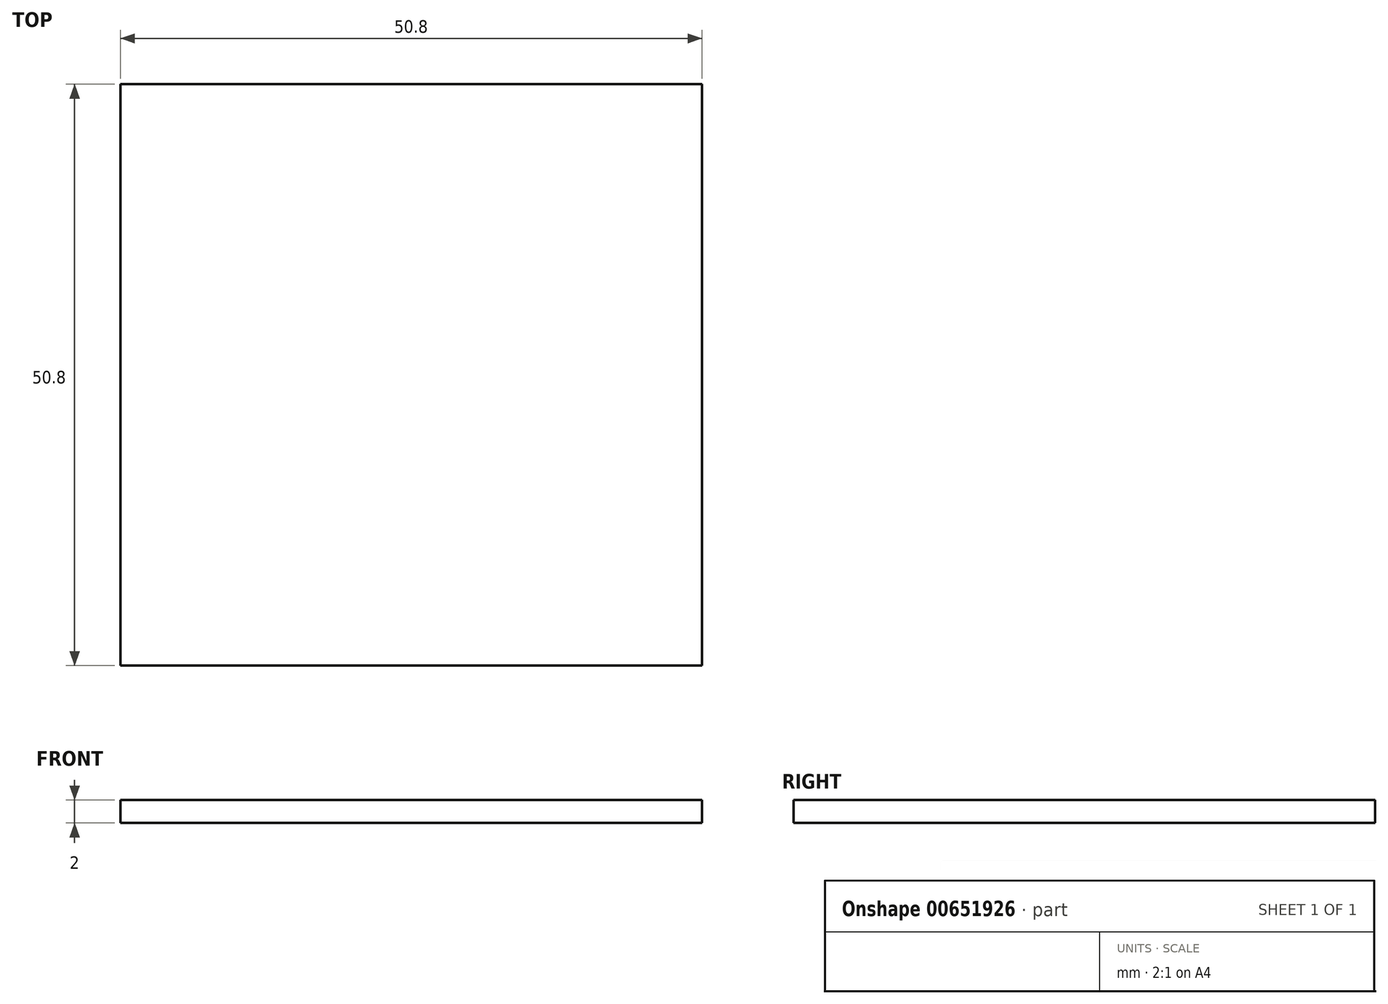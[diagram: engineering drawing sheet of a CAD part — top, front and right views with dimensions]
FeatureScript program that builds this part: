
annotation { "Feature Type Name" : "Feature", "Feature Type Description" : "" }
export const myFeature = defineFeature(function(context is Context, id is Id, definition is map)
    precondition{}
    {
        {
            var Q0;
            Q0=qCreatedBy(makeId("Top.planeOp"),FACE);
            var sketch = newSketch(context, id + "F0", { "sketchPlane" : qUnion([Q0])});
            skLineSegment(sketch, "E0.bottom", {"start": v(-29.76, 26.16) * mm, "end": v(21.04, 26.16) * mm});
            skLineSegment(sketch, "E0.top", {"start": v(-29.76, -24.64) * mm, "end": v(21.04, -24.64) * mm});
            skLineSegment(sketch, "E0.left", {"start": v(-29.76, 26.16) * mm, "end": v(-29.76, -24.64) * mm});
            skLineSegment(sketch, "E0.right", {"start": v(21.04, 26.16) * mm, "end": v(21.04, -24.64) * mm});
            skSolve(sketch);
        }
        {
            var Q0;
            Q0 = qSketchRegion(id + "F0", true);
            extrude(context, id + "F1", {"entities" : qUnion([Q0]), "depth" : 2 * mm, "offsetDistance" : 25.4 * mm});
        }
    });
